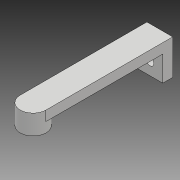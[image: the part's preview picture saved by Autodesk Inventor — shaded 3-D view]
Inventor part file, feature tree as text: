
AUTODESK INVENTOR PART (.ipt)
format: ipt  version: 2018 (Build 220112000, 112)  size: 108,544 bytes
history: native  units: mm
features: extrude x4, sketch x4, projected_geometry x4, fillet x1
ambient origin geometry x8: Origin, YZ Plane, XZ Plane, XY Plane, X Axis, Y Axis, Z Axis, Center Point
bodies: Solid1 (feature_tree)
feature tree (13):
  extrude  "Extrusion1"  Depth=5.0mm
  extrude  "Extrusion2"  Depth=17.7mm
  fillet  "Fillet1"  Radius=5.0mm
  extrude  "Extrusion3"  Depth=5.0mm TaperAngle=0.0deg
  extrude  "Extrusion4"  Depth=5.0mm
  sketch  "Sketch1"  dims[d0=13.0mm d1=5.0mm]
  sketch  "Sketch2"  dims[d2=70.4mm d3=0.0mm d4=17.7mm d5=5.0mm d6=0.0mm]
  sketch  "Sketch3"  dims[d7=6.5mm d8=5.0mm d9=0.0mm]
  sketch  "Sketch4"  dims[d10=4.0mm d11=6.35mm d12=6.5mm d13=5.0mm d14=0.0mm]
  projected_geometry  "Project Cut Edges1"
  projected_geometry  "Project Cut Edges2"
  projected_geometry  "Project Cut Edges3"
  projected_geometry  "Project Cut Edges4"
